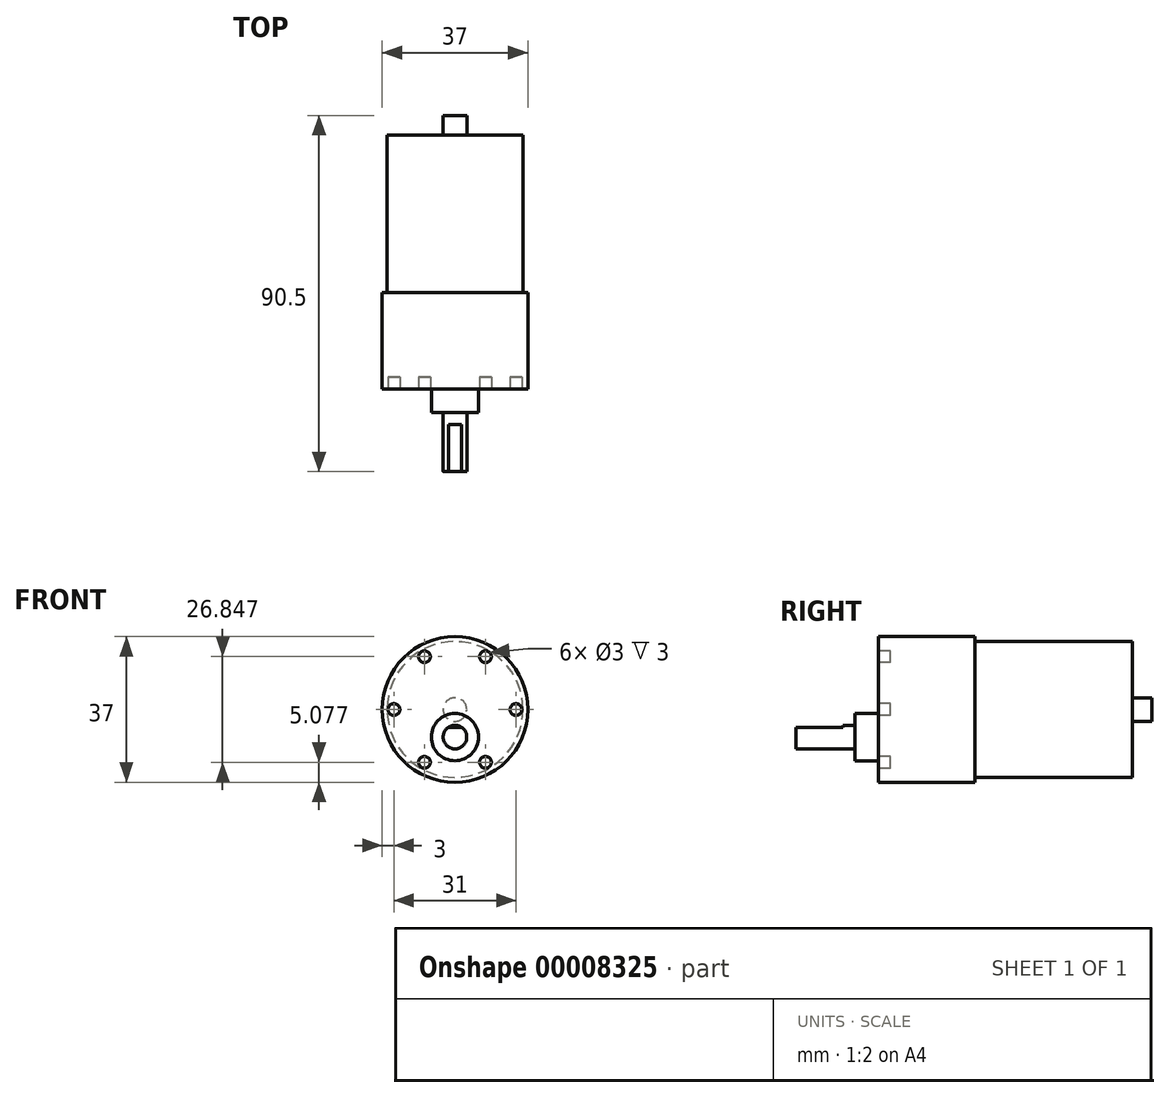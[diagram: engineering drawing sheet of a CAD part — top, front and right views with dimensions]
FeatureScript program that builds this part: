
annotation { "Feature Type Name" : "Feature", "Feature Type Description" : "" }
export const myFeature = defineFeature(function(context is Context, id is Id, definition is map)
    precondition{}
    {
        {
            var Q0;
            Q0=qCreatedBy(makeId("Front.planeOp"),FACE);
            var sketch = newSketch(context, id + "F0", { "sketchPlane" : qUnion([Q0])});
            skCircle(sketch, "E0", {"center": v(0, 0) * mm, "radius": 18.5 * mm});
            skSolve(sketch);
        }
        {
            var Q0;
            Q0 = qSketchRegion(id + "F0", true);
            extrude(context, id + "F1", {"entities" : qUnion([Q0]), "depth" : 24.5 * mm});
        }
        {
            var Q0;
            Q0=makeQuery(id+"F1.opExtrude","CAP_FACE",FACE,{"disambiguationData":[OSD([sQuery(id+"F0.wireOp",EDGE,"E0")])],"isStart":true});
            var sketch = newSketch(context, id + "F2", { "sketchPlane" : qUnion([Q0])});
            skCircle(sketch, "E1", {"center": v(0, 0) * mm, "radius": 17.25 * mm});
            skSolve(sketch);
        }
        {
            var Q0;
            Q0 = qSketchRegion(id + "F2", true);
            extrude(context, id + "F3", {"entities" : qUnion([Q0]), "operationType" : NewBodyOperationType.ADD, "depth" : 40 * mm});
        }
        {
            var Q0;
            Q0=makeQuery(id+"F3.opExtrude","CAP_FACE",FACE,{"disambiguationData":[OSD([sQuery(id+"F2.wireOp",EDGE,"E1")])],"isStart":false});
            var sketch = newSketch(context, id + "F4", { "sketchPlane" : qUnion([Q0])});
            skCircle(sketch, "E2", {"center": v(0, 0) * mm, "radius": 3 * mm});
            skSolve(sketch);
        }
        {
            var Q0;
            Q0 = qSketchRegion(id + "F4", true);
            extrude(context, id + "F5", {"entities" : qUnion([Q0]), "operationType" : NewBodyOperationType.ADD, "depth" : 5 * mm});
        }
        {
            var Q0;
            Q0=makeQuery(id+"F1.opExtrude","CAP_FACE",FACE,{"disambiguationData":[OSD([sQuery(id+"F0.wireOp",EDGE,"E0")])],"isStart":false});
            var sketch = newSketch(context, id + "F6", { "sketchPlane" : qUnion([Q0])});
            skCircle(sketch, "E3.cCircle", {"center": v(0, 0) * mm, "radius": 15.5 * mm, "construction": true});
            skLineSegment(sketch, "E3.0", {"start": v(7.75, 13.42) * mm, "end": v(15.5, 0) * mm, "construction": true});
            skLineSegment(sketch, "E3.1", {"start": v(15.5, 0) * mm, "end": v(7.75, -13.42) * mm, "construction": true});
            skLineSegment(sketch, "E3.2", {"start": v(7.75, -13.42) * mm, "end": v(-7.75, -13.42) * mm, "construction": true});
            skLineSegment(sketch, "E3.3", {"start": v(-7.75, -13.42) * mm, "end": v(-15.5, 0) * mm, "construction": true});
            skLineSegment(sketch, "E3.4", {"start": v(-15.5, 0) * mm, "end": v(-7.75, 13.42) * mm, "construction": true});
            skLineSegment(sketch, "E3.5", {"start": v(-7.75, 13.42) * mm, "end": v(7.75, 13.42) * mm, "construction": true});
            skCircle(sketch, "E4", {"center": v(7.75, 13.42) * mm, "radius": 1.5 * mm});
            skCircle(sketch, "E5", {"center": v(-7.75, 13.42) * mm, "radius": 1.5 * mm});
            skCircle(sketch, "E6", {"center": v(-15.5, 0) * mm, "radius": 1.5 * mm});
            skCircle(sketch, "E7", {"center": v(-7.75, -13.42) * mm, "radius": 1.5 * mm});
            skCircle(sketch, "E8", {"center": v(7.75, -13.42) * mm, "radius": 1.5 * mm});
            skCircle(sketch, "E9", {"center": v(15.5, 0) * mm, "radius": 1.5 * mm});
            skSolve(sketch);
        }
        {
            var Q0;
            Q0 = qSketchRegion(id + "F6", true);
            extrude(context, id + "F7", {"entities" : qUnion([Q0]), "operationType" : NewBodyOperationType.REMOVE, "oppositeDirection" : true, "depth" : 3 * mm});
        }
        {
            var Q0;
            Q0=makeQuery(id+"F1.opExtrude","CAP_FACE",FACE,{"disambiguationData":[OSD([sQuery(id+"F0.wireOp",EDGE,"E0")])],"isStart":false});
            var sketch = newSketch(context, id + "F8", { "sketchPlane" : qUnion([Q0])});
            skLineSegment(sketch, "E10", {"start": v(0, 18.5) * mm, "end": v(0, -18.5) * mm, "construction": true});
            skCircle(sketch, "E11", {"center": v(0, -7) * mm, "radius": 6 * mm});
            skPoint(sketch, "E12", {"position": v(0, 0) * mm});
            skSolve(sketch);
        }
        {
            var Q0;
            Q0 = qSketchRegion(id + "F8", true);
            extrude(context, id + "F9", {"entities" : qUnion([Q0]), "operationType" : NewBodyOperationType.ADD, "depth" : 6 * mm});
        }
        {
            var Q0;
            Q0=makeQuery(id+"F9.opExtrude","CAP_FACE",FACE,{"disambiguationData":[OSD([sQuery(id+"F8.wireOp",EDGE,"E11")])],"isStart":false});
            var sketch = newSketch(context, id + "F10", { "sketchPlane" : qUnion([Q0])});
            skCircle(sketch, "E13", {"center": v(0, -7) * mm, "radius": 3 * mm});
            skSolve(sketch);
        }
        {
            var Q0;
            Q0 = qSketchRegion(id + "F10", true);
            var Q1;
            Q1=makeQuery(id+"F1.opExtrude","CAP_FACE",FACE,{"disambiguationData":[OSD([sQuery(id+"F0.wireOp",EDGE,"E0")])],"isStart":false});
            extrude(context, id + "F11", {"entities" : qUnion([Q0]), "operationType" : NewBodyOperationType.ADD, "endBoundEntity" : qUnion([Q1]), "depth" : 15 * mm});
        }
        {
            var Q0;
            Q0=makeQuery(id+"F11.opExtrude","CAP_FACE",FACE,{"disambiguationData":[OSD([sQuery(id+"F10.wireOp",EDGE,"E13")])],"isStart":false});
            var sketch = newSketch(context, id + "F12", { "sketchPlane" : qUnion([Q0])});
            skLineSegment(sketch, "E14", {"start": v(-1.66, -4.5) * mm, "end": v(1.66, -4.5) * mm});
            skArc(sketch, "E15.0", {"start": v(1.66, -4.5) * mm, "mid": v(0, -4) * mm, "end": v(-1.66, -4.5) * mm});
            skLineSegment(sketch, "E16", {"start": v(0, -4.5) * mm, "end": v(0, -10) * mm, "construction": true});
            skSolve(sketch);
        }
        {
            var Q0;
            Q0 = qSketchRegion(id + "F12", true);
            extrude(context, id + "F13", {"entities" : qUnion([Q0]), "operationType" : NewBodyOperationType.REMOVE, "oppositeDirection" : true, "depth" : 12 * mm});
        }
    });
